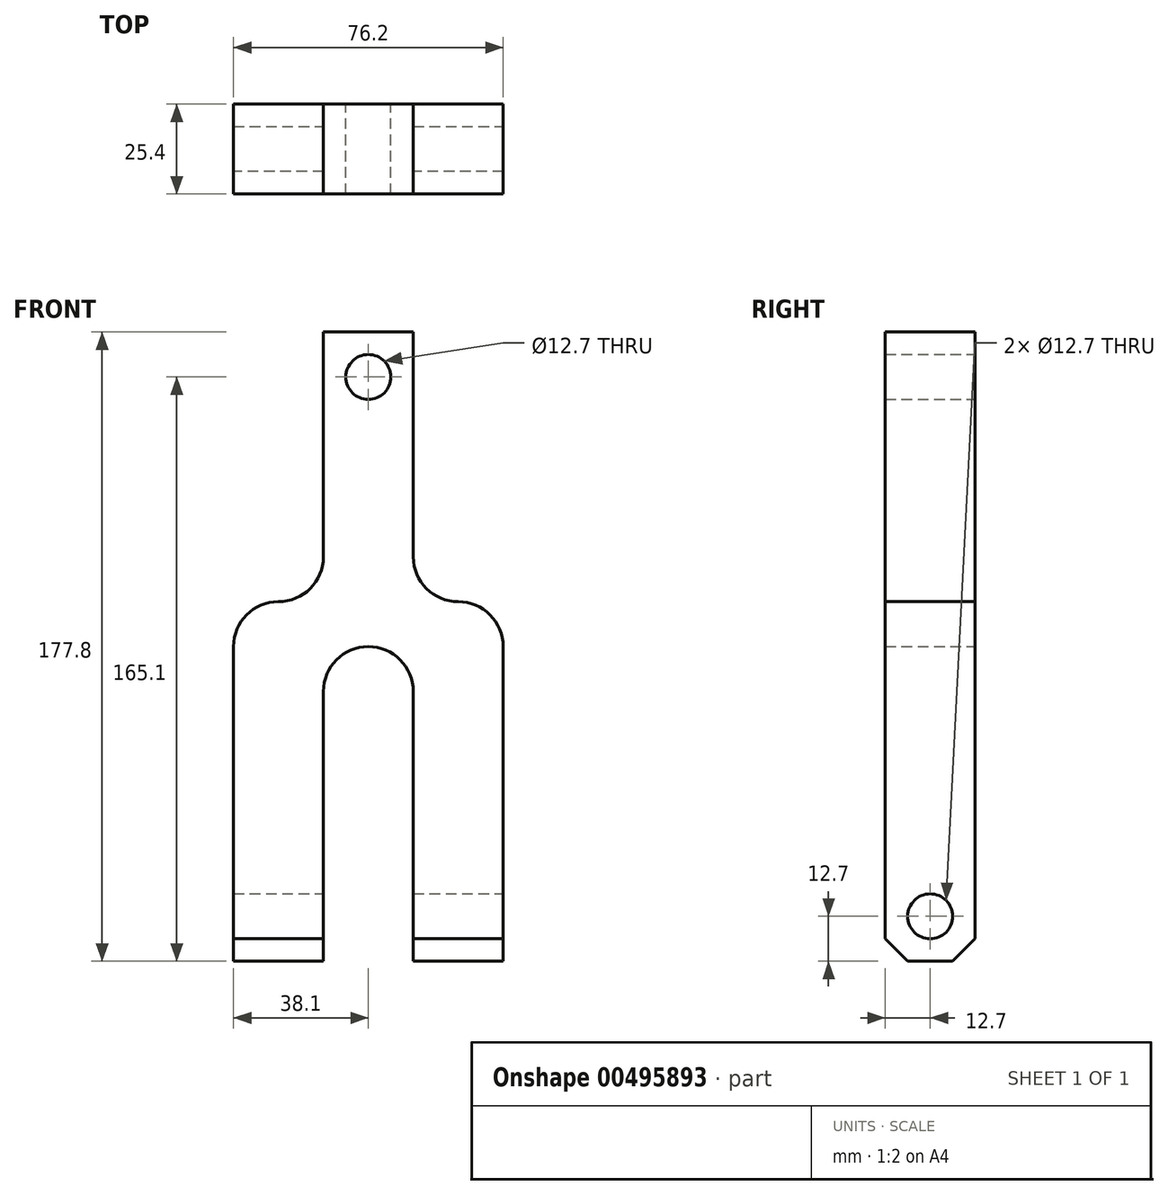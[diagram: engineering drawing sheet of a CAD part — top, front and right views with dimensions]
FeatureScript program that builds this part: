
annotation { "Feature Type Name" : "Feature", "Feature Type Description" : "" }
export const myFeature = defineFeature(function(context is Context, id is Id, definition is map)
    precondition{}
    {
        {
            var Q0;
            Q0=qCreatedBy(makeId("Front.planeOp"),FACE);
            var sketch = newSketch(context, id + "F0", { "sketchPlane" : qUnion([Q0])});
            skLineSegment(sketch, "E0.bottom", {"start": v(12.7, 38.1) * mm, "end": v(-12.7, 38.1) * mm});
            skLineSegment(sketch, "E0.left", {"start": v(12.7, 38.1) * mm, "end": v(12.7, -25.4) * mm});
            skLineSegment(sketch, "E0.right", {"start": v(-12.7, 38.1) * mm, "end": v(-12.7, -25.4) * mm});
            skPoint(sketch, "E0.middle", {"position": v(0, 0) * mm});
            skLineSegment(sketch, "E1.bottom", {"start": v(-25.4, -38.1) * mm, "end": v(-25.4, -38.1) * mm});
            skLineSegment(sketch, "E1.top", {"start": v(-12.7, -139.7) * mm, "end": v(-38.1, -139.7) * mm});
            skLineSegment(sketch, "E1.right", {"start": v(-38.1, -50.8) * mm, "end": v(-38.1, -139.7) * mm});
            skLineSegment(sketch, "E2.bottom", {"start": v(25.4, -38.1) * mm, "end": v(25.4, -38.1) * mm});
            skLineSegment(sketch, "E2.top", {"start": v(12.7, -139.7) * mm, "end": v(38.1, -139.7) * mm});
            skLineSegment(sketch, "E2.right", {"start": v(38.1, -50.8) * mm, "end": v(38.1, -139.7) * mm});
            skCircle(sketch, "E3", {"center": v(0, 25.4) * mm, "radius": 6.35 * mm});
            skLineSegment(sketch, "E4", {"start": v(-12.7, -63.5) * mm, "end": v(-12.7, -139.7) * mm});
            skLineSegment(sketch, "E5", {"start": v(12.7, -139.7) * mm, "end": v(12.7, -63.5) * mm});
            skArc(sketch, "E6", {"start": v(-12.7, -63.5) * mm, "mid": v(0, -50.8) * mm, "end": v(12.7, -63.5) * mm});
            skPoint(sketch, "E7.visualSharp", {"position": v(-38.1, -38.1) * mm});
            skArc(sketch, "E7.filletArc", {"start": v(-25.4, -38.1) * mm, "mid": v(-34.38, -41.82) * mm, "end": v(-38.1, -50.8) * mm});
            skPoint(sketch, "E8.visualSharp", {"position": v(-12.7, -38.1) * mm});
            skArc(sketch, "E8.filletArc", {"start": v(-25.4, -38.1) * mm, "mid": v(-16.42, -34.38) * mm, "end": v(-12.7, -25.4) * mm});
            skPoint(sketch, "E9.visualSharp", {"position": v(12.7, -38.1) * mm});
            skArc(sketch, "E9.filletArc", {"start": v(12.7, -25.4) * mm, "mid": v(16.42, -34.38) * mm, "end": v(25.4, -38.1) * mm});
            skPoint(sketch, "E10.visualSharp", {"position": v(38.1, -38.1) * mm});
            skArc(sketch, "E10.filletArc", {"start": v(38.1, -50.8) * mm, "mid": v(34.38, -41.82) * mm, "end": v(25.4, -38.1) * mm});
            skSolve(sketch);
        }
        {
            var Q0;
            Q0 = qSketchRegion(id + "F0", true);
            extrude(context, id + "F1", {"entities" : qUnion([Q0]), "endBound" : BoundingType.SYMMETRIC, "depth" : 25.4 * mm});
        }
        {
            var Q0;
            Q0=makeQuery(id+"F1.opExtrude","CAP_EDGE",EDGE,{"disambiguationData":[OSD([sQuery(id+"F0.wireOp",EDGE,"E1.top")])],"isStart":true});
            var Q1;
            Q1=makeQuery(id+"F1.opExtrude","CAP_EDGE",EDGE,{"disambiguationData":[OSD([sQuery(id+"F0.wireOp",EDGE,"E1.top")])],"isStart":false});
            var Q2;
            Q2=makeQuery(id+"F1.opExtrude","CAP_EDGE",EDGE,{"disambiguationData":[OSD([sQuery(id+"F0.wireOp",EDGE,"E2.top")])],"isStart":false});
            var Q3;
            Q3=makeQuery(id+"F1.opExtrude","CAP_EDGE",EDGE,{"disambiguationData":[OSD([sQuery(id+"F0.wireOp",EDGE,"E2.top")])],"isStart":true});
            chamfer(context, id + "F2", {"entities" : qUnion([Q0, Q1, Q2, Q3]), "width" : 6.35 * mm, "tangentPropagation" : true});
        }
        {
            var Q0;
            Q0=makeQuery(id+"F1.opExtrude","SWEPT_FACE",FACE,{"disambiguationData":[OSD([sQuery(id+"F0.wireOp",EDGE,"E2.right")])]});
            var sketch = newSketch(context, id + "F3", { "sketchPlane" : qUnion([Q0])});
            skCircle(sketch, "E11", {"center": v(0, -127) * mm, "radius": 6.35 * mm});
            skSolve(sketch);
        }
        {
            var Q0;
            Q0=makeQuery(id+"F3.imprint","IMPRINT",FACE,{"disambiguationData":[TD([[makeQuery(id+"F3.imprint","IMPRINT",EDGE,{"derivedFrom":sQuery(id+"F3.wireOp",EDGE,"E11")}),1.0]])]});
            extrude(context, id + "F4", {"entities" : qUnion([Q0]), "operationType" : NewBodyOperationType.REMOVE, "oppositeDirection" : true, "depth" : 76.2 * mm});
        }
    });
